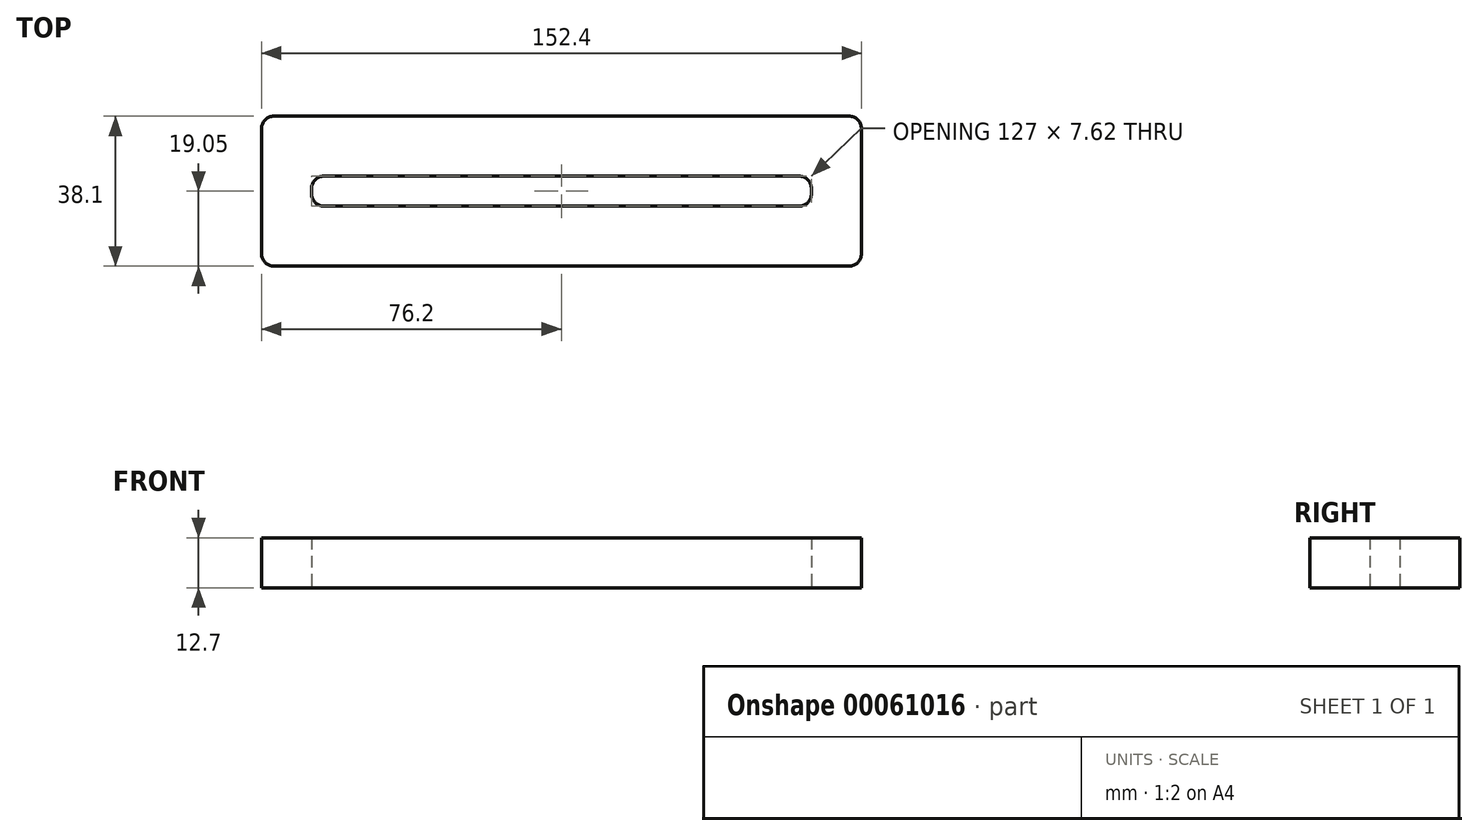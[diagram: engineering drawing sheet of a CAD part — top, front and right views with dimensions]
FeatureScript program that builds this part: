
annotation { "Feature Type Name" : "Feature", "Feature Type Description" : "" }
export const myFeature = defineFeature(function(context is Context, id is Id, definition is map)
    precondition{}
    {
        {
            var Q0;
            Q0=qCreatedBy(makeId("Top.planeOp"),FACE);
            var sketch = newSketch(context, id + "F0", { "sketchPlane" : qUnion([Q0])});
            skLineSegment(sketch, "E0.bottom", {"start": v(3.18, 0) * mm, "end": v(149.22, 0) * mm});
            skLineSegment(sketch, "E0.top", {"start": v(3.18, -38.1) * mm, "end": v(149.22, -38.1) * mm});
            skLineSegment(sketch, "E0.left", {"start": v(0, -3.18) * mm, "end": v(0, -34.93) * mm});
            skLineSegment(sketch, "E0.right", {"start": v(152.4, -3.18) * mm, "end": v(152.4, -34.93) * mm});
            skPoint(sketch, "E1.visualSharp", {"position": v(0, 0) * mm});
            skArc(sketch, "E1.filletArc", {"start": v(3.18, 0) * mm, "mid": v(0.93, -0.93) * mm, "end": v(0, -3.18) * mm});
            skPoint(sketch, "E2.visualSharp", {"position": v(0, -38.1) * mm});
            skArc(sketch, "E2.filletArc", {"start": v(0, -34.93) * mm, "mid": v(0.93, -37.17) * mm, "end": v(3.18, -38.1) * mm});
            skPoint(sketch, "E3.visualSharp", {"position": v(152.4, 0) * mm});
            skArc(sketch, "E3.filletArc", {"start": v(152.4, -3.18) * mm, "mid": v(151.47, -0.93) * mm, "end": v(149.22, 0) * mm});
            skPoint(sketch, "E4.visualSharp", {"position": v(152.4, -38.1) * mm});
            skArc(sketch, "E4.filletArc", {"start": v(149.22, -38.1) * mm, "mid": v(151.47, -37.17) * mm, "end": v(152.4, -34.93) * mm});
            skLineSegment(sketch, "E5.bottom", {"start": v(15.88, -15.24) * mm, "end": v(136.53, -15.24) * mm});
            skLineSegment(sketch, "E5.top", {"start": v(15.88, -22.86) * mm, "end": v(136.53, -22.86) * mm});
            skLineSegment(sketch, "E5.left", {"start": v(12.7, -18.41) * mm, "end": v(12.7, -19.68) * mm});
            skLineSegment(sketch, "E5.right", {"start": v(139.7, -18.41) * mm, "end": v(139.7, -19.68) * mm});
            skPoint(sketch, "E6.visualSharp", {"position": v(12.7, -22.86) * mm});
            skArc(sketch, "E6.filletArc", {"start": v(12.7, -19.68) * mm, "mid": v(13.63, -21.93) * mm, "end": v(15.88, -22.86) * mm});
            skPoint(sketch, "E7.visualSharp", {"position": v(12.7, -15.24) * mm});
            skArc(sketch, "E7.filletArc", {"start": v(15.88, -15.24) * mm, "mid": v(13.63, -16.17) * mm, "end": v(12.7, -18.41) * mm});
            skPoint(sketch, "E8.visualSharp", {"position": v(139.7, -15.24) * mm});
            skArc(sketch, "E8.filletArc", {"start": v(139.7, -18.41) * mm, "mid": v(138.77, -16.17) * mm, "end": v(136.53, -15.24) * mm});
            skPoint(sketch, "E9.visualSharp", {"position": v(139.7, -22.86) * mm});
            skArc(sketch, "E9.filletArc", {"start": v(136.53, -22.86) * mm, "mid": v(138.77, -21.93) * mm, "end": v(139.7, -19.68) * mm});
            skSolve(sketch);
        }
        {
            var Q0;
            Q0 = qSketchRegion(id + "F0", true);
            extrude(context, id + "F1", {"entities" : qUnion([Q0]), "depth" : 12.7 * mm});
        }
    });
